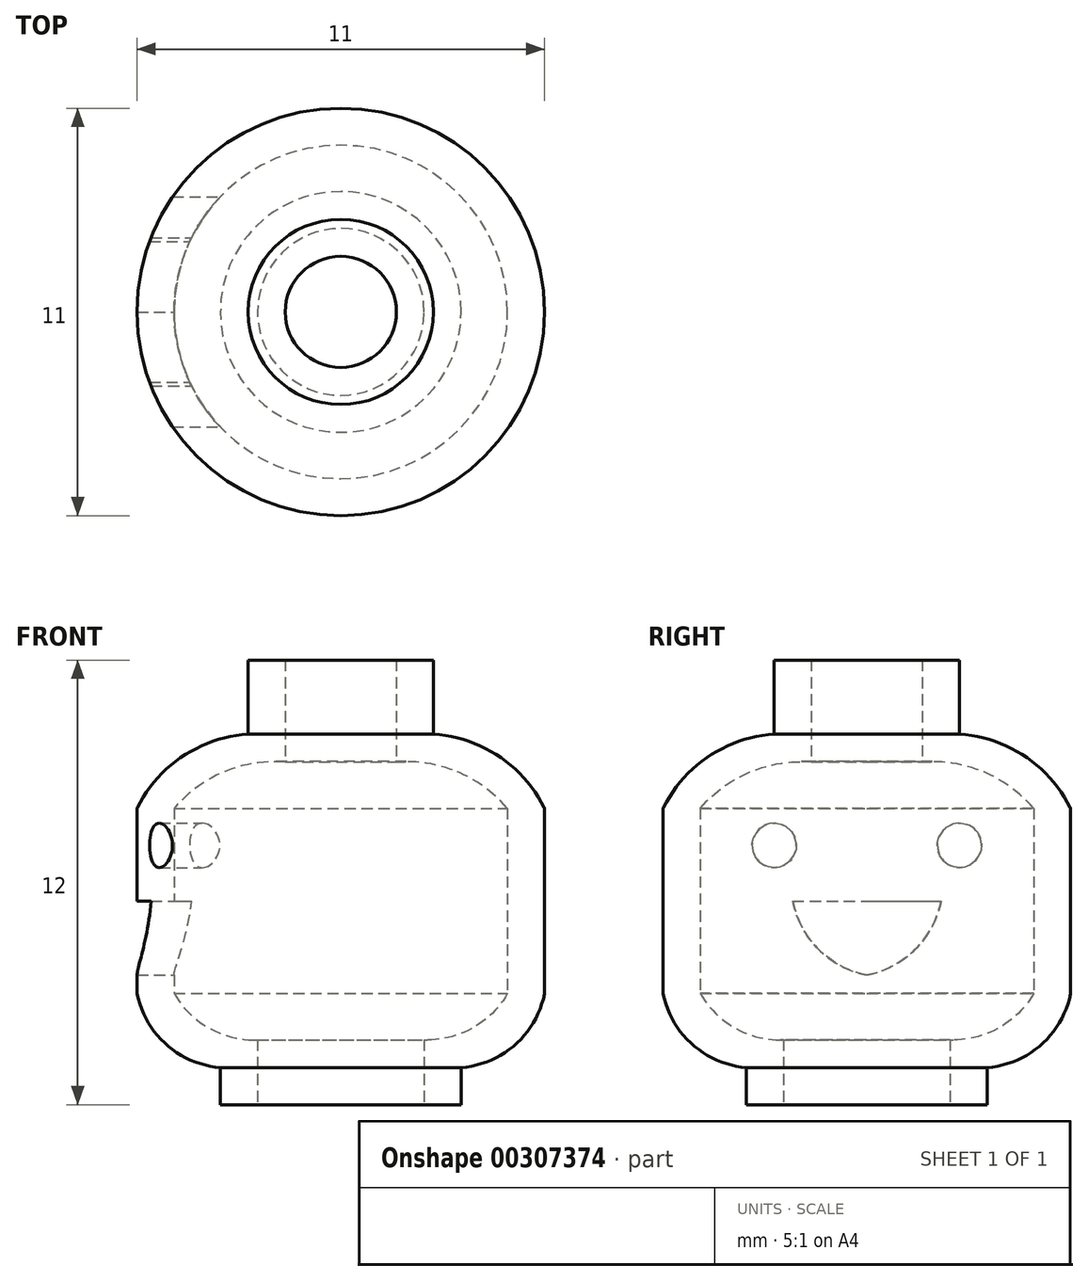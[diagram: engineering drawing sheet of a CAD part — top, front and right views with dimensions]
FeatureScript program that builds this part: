
annotation { "Feature Type Name" : "Feature", "Feature Type Description" : "" }
export const myFeature = defineFeature(function(context is Context, id is Id, definition is map)
    precondition{}
    {
        {
            var Q0;
            Q0=qCreatedBy(makeId("Front.planeOp"),FACE);
            var sketch = newSketch(context, id + "F0", { "sketchPlane" : qUnion([Q0])});
            skLineSegment(sketch, "E0", {"start": v(0, 0) * mm, "end": v(0, 6) * mm, "construction": true});
            skLineSegment(sketch, "E1", {"start": v(0, 0) * mm, "end": v(0, -6) * mm, "construction": true});
            skLineSegment(sketch, "E2", {"start": v(0, 6) * mm, "end": v(0, 4) * mm});
            skLineSegment(sketch, "E3", {"start": v(0, 0) * mm, "end": v(0, 4) * mm});
            skLineSegment(sketch, "E4", {"start": v(0, 6) * mm, "end": v(2.5, 6) * mm});
            skLineSegment(sketch, "E5", {"start": v(2.5, 6) * mm, "end": v(2.5, 4) * mm});
            skLineSegment(sketch, "E6", {"start": v(0, 2) * mm, "end": v(5.5, 2) * mm, "construction": true});
            skArc(sketch, "E7", {"start": v(5.5, 2) * mm, "mid": v(4.27, 3.4) * mm, "end": v(2.5, 4) * mm});
            skLineSegment(sketch, "E8", {"start": v(0, -6) * mm, "end": v(0, -5) * mm});
            skLineSegment(sketch, "E9", {"start": v(0, 0) * mm, "end": v(0, -5) * mm});
            skLineSegment(sketch, "E10", {"start": v(0, -3) * mm, "end": v(5.5, -3) * mm, "construction": true});
            skLineSegment(sketch, "E11", {"start": v(0, -6) * mm, "end": v(3.25, -6) * mm});
            skLineSegment(sketch, "E12", {"start": v(3.25, -6) * mm, "end": v(3.25, -5) * mm});
            skArc(sketch, "E13", {"start": v(3.25, -5) * mm, "mid": v(4.7, -4.38) * mm, "end": v(5.5, -3) * mm});
            skLineSegment(sketch, "E14", {"start": v(5.5, -3) * mm, "end": v(5.5, 2) * mm});
            skLineSegment(sketch, "E15", {"start": v(1.8, 6) * mm, "end": v(1.8, 5) * mm, "construction": true});
            skLineSegment(sketch, "E16", {"start": v(1.8, 5) * mm, "end": v(2.5, 5) * mm, "construction": true});
            skLineSegment(sketch, "E17", {"start": v(2.5, 5) * mm, "end": v(1.5, 5) * mm, "construction": true});
            skLineSegment(sketch, "E18", {"start": v(1.5, 6) * mm, "end": v(1.5, 3.25) * mm});
            skLineSegment(sketch, "E19", {"start": v(5.5, -1.54) * mm, "end": v(4.5, -1.54) * mm, "construction": true});
            skLineSegment(sketch, "E20", {"start": v(4.5, -3) * mm, "end": v(4.5, 2) * mm, "construction": true});
            skArc(sketch, "E21", {"start": v(4.5, 2) * mm, "mid": v(3.15, 2.98) * mm, "end": v(1.5, 3.25) * mm});
            skLineSegment(sketch, "E22", {"start": v(4.5, 2) * mm, "end": v(4.5, -3) * mm});
            skLineSegment(sketch, "E23", {"start": v(3.25, -5) * mm, "end": v(2.25, -5) * mm, "construction": true});
            skLineSegment(sketch, "E24", {"start": v(2.25, -6) * mm, "end": v(2.25, -4.25) * mm});
            skArc(sketch, "E25", {"start": v(2.25, -4.25) * mm, "mid": v(3.55, -3.94) * mm, "end": v(4.5, -3) * mm});
            skSolve(sketch);
        }
        {
            var Q0;
            {var subQ2=sQuery(id+"F0.wireOp",EDGE,"E5");Q0=makeQuery(id+"F0.imprint","IMPRINT",FACE,{"disambiguationData":[TD([[makeQuery(id+"F0.imprint","IMPRINT",EDGE,{"derivedFrom":subQ2}),-1.0]])]});}
            var Q1;
            Q1=sQuery(id+"F0.wireOp",EDGE,"E3");
            revolve(context, id + "F1", {"entities" : qUnion([Q0]), "axis" : qUnion([Q1]), "revolveType" : RevolveType.FULL});
        }
        {
            var Q0;
            Q0=makeQuery(id+"F1.opRevolve","SWEPT_EDGE",EDGE,{"disambiguationData":[OSD([sQuery(id+"F0.wireOp",EDGE,"E7"),sQuery(id+"F0.wireOp",EDGE,"E14")])]});
            var Q1;
            Q1=makeQuery(id+"F1.opRevolve","SWEPT_EDGE",EDGE,{"disambiguationData":[OSD([sQuery(id+"F0.wireOp",EDGE,"E13"),sQuery(id+"F0.wireOp",EDGE,"E14")])]});
            fillet(context, id + "F2", {"entities" : qUnion([Q0, Q1]), "radius" : 0.1 * mm, "tangentPropagation" : true, "allowEdgeOverflow" : false});
        }
        {
            var Q0;
            Q0=qCreatedBy(makeId("Right.planeOp"),FACE);
            var sketch = newSketch(context, id + "F3", { "sketchPlane" : qUnion([Q0])});
            skLineSegment(sketch, "E26.bottom", {"start": v(0, 0) * mm, "end": v(-5, 0) * mm, "construction": true});
            skLineSegment(sketch, "E26.top", {"start": v(0, 2) * mm, "end": v(-5, 2) * mm, "construction": true});
            skLineSegment(sketch, "E26.left", {"start": v(0, 0) * mm, "end": v(0, 2) * mm, "construction": true});
            skLineSegment(sketch, "E26.right", {"start": v(-5, 0) * mm, "end": v(-5, 2) * mm, "construction": true});
            skLineSegment(sketch, "E27", {"start": v(0, 0) * mm, "end": v(-5, 2) * mm, "construction": true});
            skLineSegment(sketch, "E28", {"start": v(-5, 0) * mm, "end": v(0, 2) * mm, "construction": true});
            skCircle(sketch, "E29", {"center": v(-2.5, 1) * mm, "radius": 0.6 * mm});
            skCircle(sketch, "E30.MirrorC", {"center": v(2.5, 1) * mm, "radius": 0.6 * mm});
            skLineSegment(sketch, "E31.bottom", {"start": v(0, 0) * mm, "end": v(5, 0) * mm, "construction": true});
            skLineSegment(sketch, "E31.top", {"start": v(0, -3) * mm, "end": v(5, -3) * mm, "construction": true});
            skLineSegment(sketch, "E31.left", {"start": v(0, 0) * mm, "end": v(0, -3) * mm, "construction": true});
            skLineSegment(sketch, "E31.right", {"start": v(5, 0) * mm, "end": v(5, -3) * mm, "construction": true});
            skLineSegment(sketch, "E32", {"start": v(0, -1.5) * mm, "end": v(0, -2.5) * mm, "construction": true});
            skLineSegment(sketch, "E33", {"start": v(0, -2.5) * mm, "end": v(0, -1.5) * mm, "construction": true});
            skLineSegment(sketch, "E34", {"start": v(0, -1.5) * mm, "end": v(0, -0.5) * mm, "construction": true});
            skLineSegment(sketch, "E35", {"start": v(0, -0.5) * mm, "end": v(2, -0.5) * mm});
            skArc(sketch, "E36", {"start": v(0, -2.5) * mm, "mid": v(1.31, -1.81) * mm, "end": v(2, -0.5) * mm});
            skLineSegment(sketch, "E37", {"start": v(0, -0.5) * mm, "end": v(0, -2.5) * mm});
            skArc(sketch, "E38.MirrorCS", {"start": v(0, -2.5) * mm, "mid": v(-1.31, -1.81) * mm, "end": v(-2, -0.5) * mm});
            skLineSegment(sketch, "E39.MirrorCS", {"start": v(0, -0.5) * mm, "end": v(-2, -0.5) * mm});
            skSolve(sketch);
        }
        {
            var Q0;
            Q0 = qSketchRegion(id + "F3", true);
            extrude(context, id + "F4", {"entities" : qUnion([Q0]), "operationType" : NewBodyOperationType.REMOVE, "oppositeDirection" : true, "depth" : 25 * mm, "offsetDistance" : 25 * mm});
        }
    });
